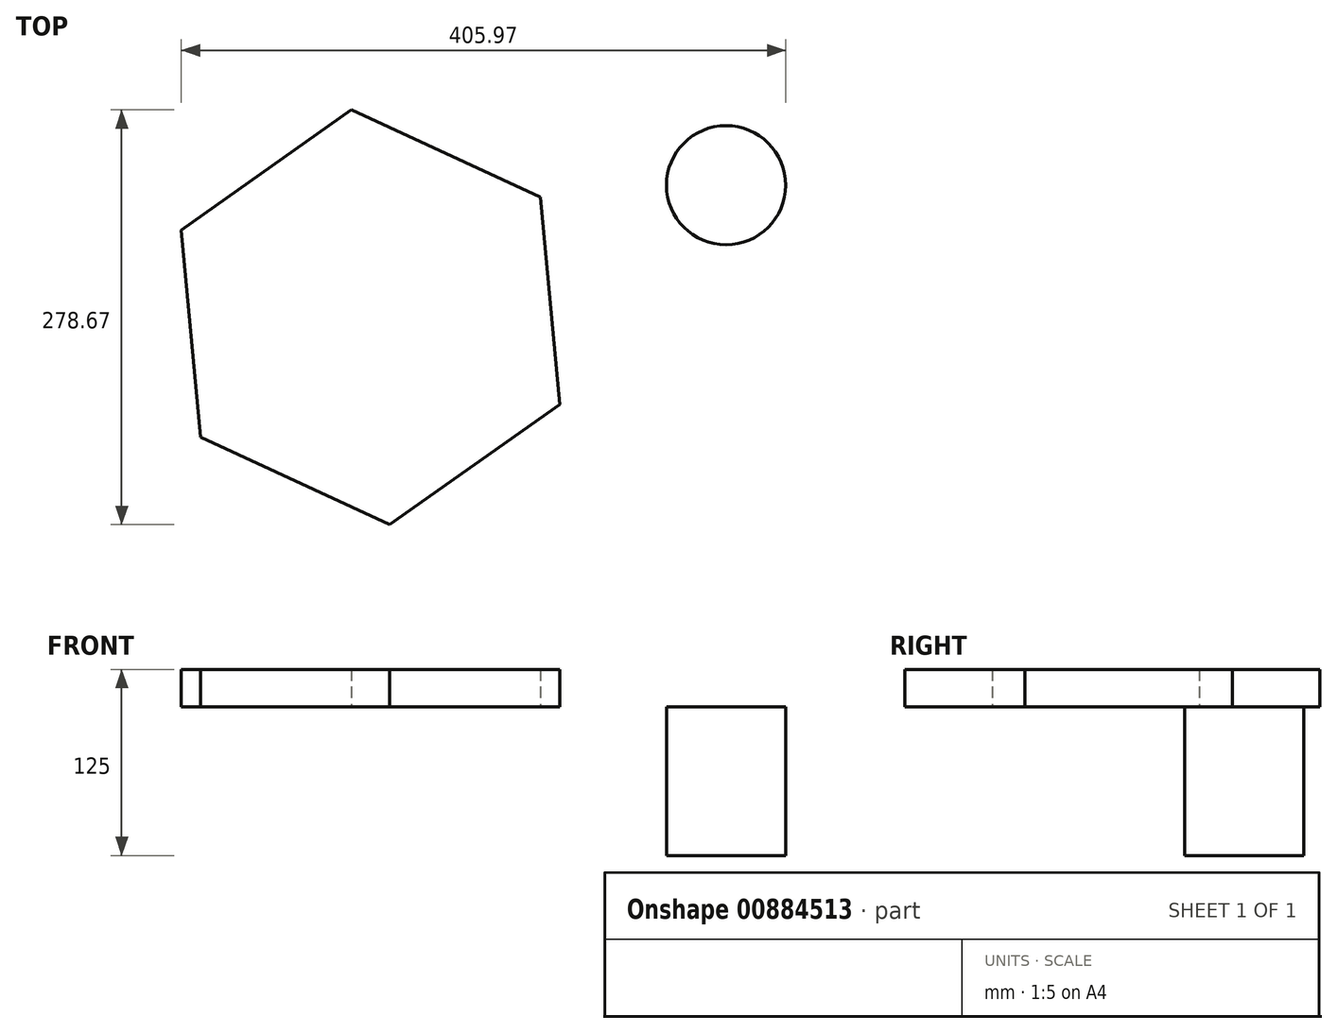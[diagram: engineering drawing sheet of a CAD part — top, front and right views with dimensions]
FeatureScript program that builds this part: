
annotation { "Feature Type Name" : "Feature", "Feature Type Description" : "" }
export const myFeature = defineFeature(function(context is Context, id is Id, definition is map)
    precondition{}
    {
        {
            var Q0;
            Q0=qCreatedBy(makeId("Top.planeOp"),FACE);
            var sketch = newSketch(context, id + "F0", { "sketchPlane" : qUnion([Q0])});
            skCircle(sketch, "E0", {"center": v(0, 0) * mm, "radius": 40.05 * mm});
            skCircle(sketch, "E1", {"center": v(0, 0) * mm, "radius": 103.3 * mm});
            skSolve(sketch);
        }
        {
            var Q0;
            Q0=makeQuery(id+"F0.imprint","IMPRINT",FACE,{"disambiguationData":[TD([[makeQuery(id+"F0.imprint","IMPRINT",EDGE,{"derivedFrom":sQuery(id+"F0.wireOp",EDGE,"E0")}),1.0]])]});
            extrude(context, id + "F1", {"entities" : qUnion([Q0]), "depth" : 100 * mm, "offsetDistance" : 25.4 * mm});
        }
        {
            var Q0;
            Q0=makeQuery(id+"F1.opExtrude","CAP_FACE",FACE,{"disambiguationData":[OSD([sQuery(id+"F0.wireOp",EDGE,"E0")])],"isStart":false});
            var sketch = newSketch(context, id + "F2", { "sketchPlane" : qUnion([Q0])});
            skSolve(sketch);
        }
        {
            var Q0;
            Q0=makeQuery(id+"F2.imprint","IMPRINT",FACE,{"disambiguationData":[TD([[makeQuery(id+"F2.imprint","IMPRINT",EDGE,{"derivedFrom":makeQuery(id+"F1.opExtrude","CAP_EDGE",EDGE,{"disambiguationData":[OSD([sQuery(id+"F0.wireOp",EDGE,"E0")])],"isStart":false})}),1.0]])]});
            var sketch = newSketch(context, id + "F3", { "sketchPlane" : qUnion([Q0])});
            skCircle(sketch, "E2.cCircle", {"center": v(-238.86, -88.68) * mm, "radius": 139.92 * mm, "construction": true});
            skLineSegment(sketch, "E2.0", {"start": v(-353.15, -169.4) * mm, "end": v(-365.92, -30.07) * mm});
            skLineSegment(sketch, "E2.1", {"start": v(-365.92, -30.07) * mm, "end": v(-251.64, 50.66) * mm});
            skLineSegment(sketch, "E2.2", {"start": v(-251.64, 50.66) * mm, "end": v(-124.58, -7.95) * mm});
            skLineSegment(sketch, "E2.3", {"start": v(-124.58, -7.95) * mm, "end": v(-111.8, -147.28) * mm});
            skLineSegment(sketch, "E2.4", {"start": v(-111.8, -147.28) * mm, "end": v(-226.1, -228.01) * mm});
            skLineSegment(sketch, "E2.5", {"start": v(-226.1, -228.01) * mm, "end": v(-353.15, -169.4) * mm});
            skSolve(sketch);
        }
        {
            var Q0;
            Q0=makeQuery(id+"F3.imprint","IMPRINT",FACE,{"disambiguationData":[TD([[makeQuery(id+"F3.imprint","IMPRINT",EDGE,{"derivedFrom":sQuery(id+"F3.wireOp",EDGE,"E2.0")}),-1.0]])]});
            extrude(context, id + "F4", {"entities" : qUnion([Q0]), "depth" : 25 * mm, "offsetDistance" : 25.4 * mm});
        }
    });
